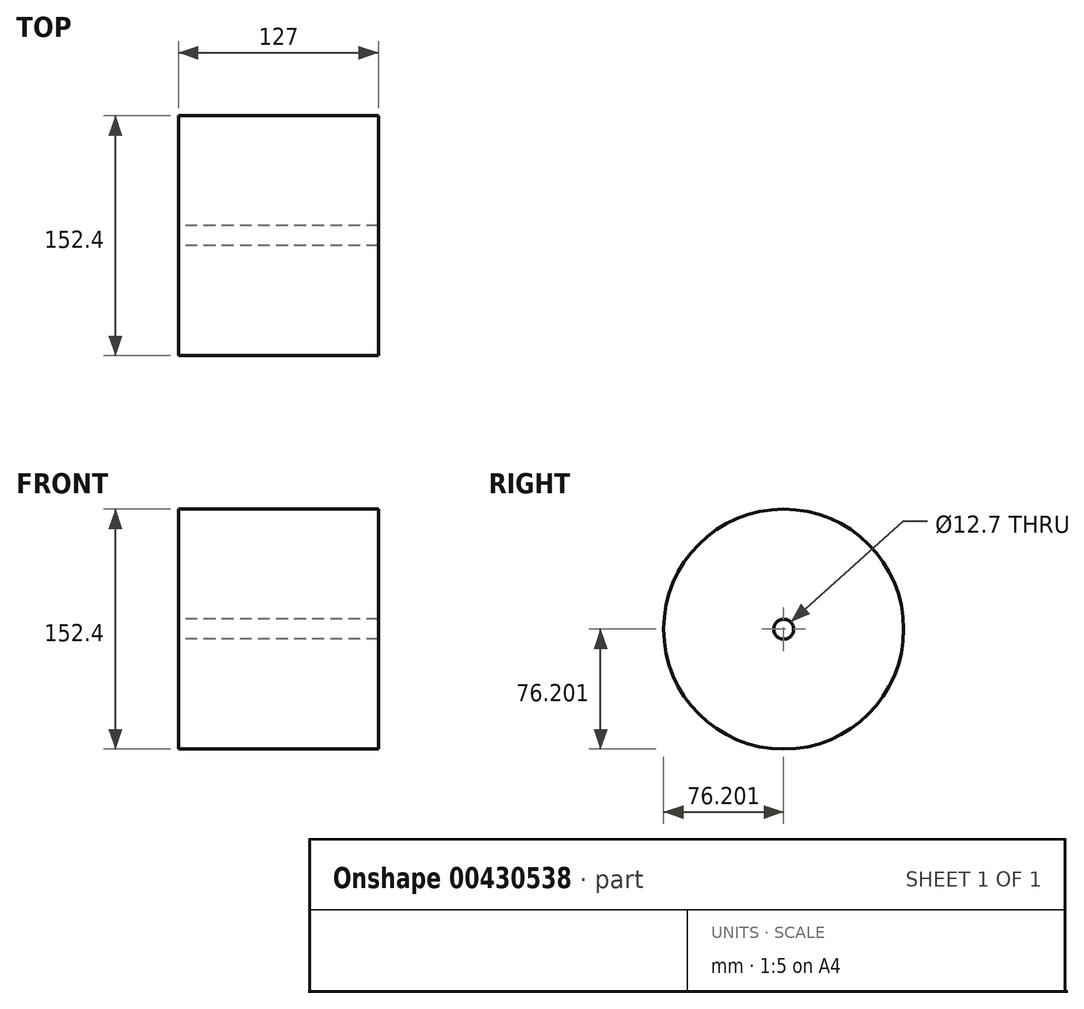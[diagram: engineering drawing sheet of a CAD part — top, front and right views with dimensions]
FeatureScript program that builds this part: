
annotation { "Feature Type Name" : "Feature", "Feature Type Description" : "" }
export const myFeature = defineFeature(function(context is Context, id is Id, definition is map)
    precondition{}
    {
        {
            var Q0;
            Q0=qCreatedBy(makeId("Right.planeOp"),FACE);
            var sketch = newSketch(context, id + "F0", { "sketchPlane" : qUnion([Q0])});
            skCircle(sketch, "E0", {"center": v(-64.66, 56.75) * mm, "radius": 76.2 * mm});
            skCircle(sketch, "E1", {"center": v(-64.66, 56.75) * mm, "radius": 6.35 * mm});
            skSolve(sketch);
        }
        {
            var Q0;
            Q0=makeQuery(id+"F0.imprint","IMPRINT",FACE,{"disambiguationData":[TD([[makeQuery(id+"F0.imprint","IMPRINT",EDGE,{"derivedFrom":sQuery(id+"F0.wireOp",EDGE,"E0")}),1.0]])]});
            extrude(context, id + "F1", {"entities" : qUnion([Q0]), "depth" : 127 * mm});
        }
    });
